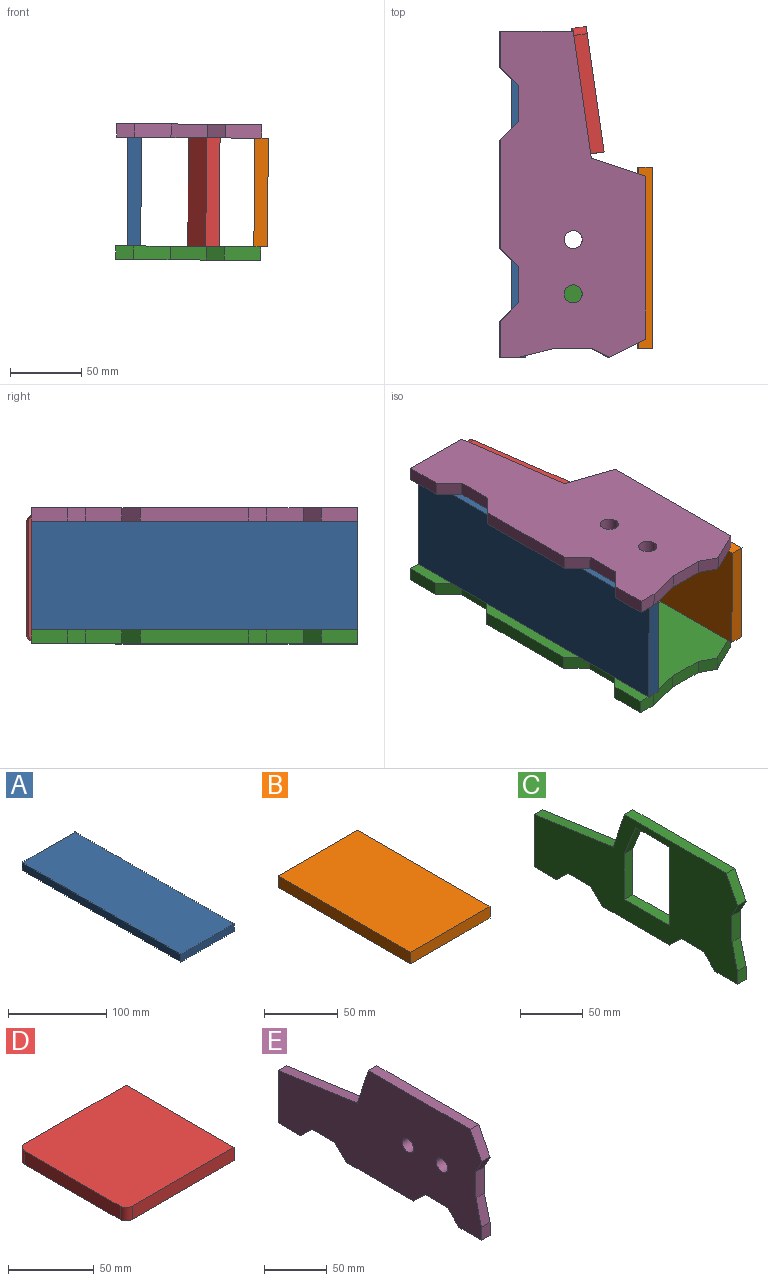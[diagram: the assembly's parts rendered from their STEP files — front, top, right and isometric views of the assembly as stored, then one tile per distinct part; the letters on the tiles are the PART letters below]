
ASSEMBLY  parts=5 mates=4
PART A: 6 faces, bbox 76.2x228.6x9.5 mm
  f0: plane 76.2x9.53mm, normal (0,-1,0), area 725.8mm2, adj f1,f3,f4,f5
  f1: plane 228.6x9.53mm, normal (1,0,0), area 2177.4mm2, adj f0,f2,f4,f5
  f2: plane 76.2x9.53mm, normal (0,1,0), area 725.8mm2, adj f1,f3,f4,f5
  f3: plane 228.6x9.53mm, normal (-1,0,0), area 2177.4mm2, adj f0,f2,f4,f5
  f4: plane 228.6x76.2mm, normal (0,0,1), area 17419.3mm2, adj f0,f1,f2,f3
  f5: plane 228.6x76.2mm, normal (0,0,-1), area 17419.3mm2, adj f0,f1,f2,f3
PART B: 6 faces, bbox 76.2x127x9.5 mm
  f0: plane 76.2x9.53mm, normal (0,1,0), area 725.8mm2, adj f1,f3,f4,f5
  f1: plane 127x9.53mm, normal (-1,0,0), area 1209.7mm2, adj f0,f2,f4,f5
  f2: plane 76.2x9.53mm, normal (0,-1,0), area 725.8mm2, adj f1,f3,f4,f5
  f3: plane 127x9.53mm, normal (1,0,0), area 1209.7mm2, adj f0,f2,f4,f5
  f4: plane 127x76.2mm, normal (0,0,1), area 9677.4mm2, adj f0,f1,f2,f3
  f5: plane 127x76.2mm, normal (0,0,-1), area 9677.4mm2, adj f0,f1,f2,f3
PART C: 25 faces, bbox 9.5x228.6x101.6 mm
  f0: plane 12.7x12.7mm, normal (0,0.71,-0.71), area 171.1mm2, adj f1,f22,f23,f24
  f1: plane 25.4x9.53mm, normal (0,0,-1), area 241.9mm2, adj f0,f2,f23,f24
  f2: plane 12.7x12.7mm, normal (0,-0.71,-0.71), area 171.1mm2, adj f1,f3,f23,f24
  f3: plane 25.4x9.53mm, normal (0,0,-1), area 241.9mm2, adj f2,f4,f23,f24
  f4: plane 50.8x9.53mm, normal (0,1,0), area 483.9mm2, adj f3,f5,f23,f24
  f5: plane 88.9x12.7mm, normal (0,0.14,0.99), area 855.4mm2, adj f4,f6,f23,f24
  f6: plane 38.1x12.7mm, normal (0,0.95,0.32), area 382.5mm2, adj f5,f7,f23,f24
  f7: plane 114.3x9.53mm, normal (0,0,1), area 1088.7mm2, adj f6,f8,f23,f24
  f8: plane 25.4x12.7mm, normal (0,-0.89,0.45), area 270.5mm2, adj f7,f9,f23,f24
  f9: plane 12.7x9.53mm, normal (0,-0.89,-0.45), area 135.2mm2, adj f8,f10,f23,f24
  f10: plane 25.4x9.53mm, normal (0,-1,0), area 241.9mm2, adj f9,f11,f23,f24
  f11: plane 25.4x9.53mm, normal (0,-0.97,0.24), area 249.4mm2, adj f10,f12,f23,f24
  f12: plane 12.7x9.53mm, normal (0,-1,0), area 121mm2, adj f11,f13,f23,f24
  f13: plane 25.4x9.53mm, normal (0,0,-1), area 241.9mm2, adj f12,f14,f23,f24
  f14: plane 12.7x12.7mm, normal (0,0.71,-0.71), area 171.1mm2, adj f13,f15,f23,f24
  f15: plane 25.4x9.53mm, normal (0,0,-1), area 241.9mm2, adj f14,f16,f23,f24
  f16: plane 12.7x12.7mm, normal (0,-0.71,-0.71), area 171.1mm2, adj f15,f22,f23,f24
  f17: plane 38.1x9.53mm, normal (0,0,-1), area 362.9mm2, adj f18,f21,f23,f24
  f18: plane 31.75x12.7mm, normal (0,-0.93,-0.37), area 325.7mm2, adj f17,f19,f23,f24
  f19: plane 44.45x9.53mm, normal (0,-1,0), area 423.4mm2, adj f18,f20,f23,f24
  f20: plane 50.8x9.53mm, normal (0,0,1), area 483.9mm2, adj f19,f21,f23,f24
  f21: plane 76.2x9.53mm, normal (0,1,0), area 725.8mm2, adj f17,f20,f23,f24
  f22: plane 76.2x9.53mm, normal (0,0,-1), area 725.8mm2, adj f0,f16,f23,f24
  f23: plane 228.6x101.6mm, normal (1,0,0), area 13951.6mm2, adj f0,f1,f2,f3,f4,f5,f6,f7
  f24: plane 228.6x101.6mm, normal (-1,0,0), area 13951.6mm2, adj f0,f1,f2,f3,f4,f5,f6,f7
PART D: 8 faces, bbox 88.9x88.9x9.5 mm
  f0: plane 83.82x9.53mm, normal (0,1,0), area 798.4mm2, adj f3,f4,f5,f6
  f1: plane 78.74x9.53mm, normal (-1,0,0), area 750mm2, adj f4,f5,f6,f7
  f2: plane 83.82x9.53mm, normal (0,-1,0), area 798.4mm2, adj f3,f4,f5,f7
  f3: plane 88.9x9.53mm, normal (1,0,0), area 846.8mm2, adj f0,f2,f4,f5
  f4: plane 88.9x88.9mm, normal (0,0,1), area 7892.1mm2, adj f0,f1,f2,f3,f6,f7
  f5: plane 88.9x88.9mm, normal (0,0,-1), area 7892.1mm2, adj f0,f1,f2,f3,f6,f7
  f6: cylinder r=5.08mm len=9.53mm, axis (0,0,1), area 76mm2, adj f0,f1,f4,f5
  f7: cylinder r=5.08mm len=9.53mm, axis (0,0,-1), area 76mm2, adj f1,f2,f4,f5
PART E: 22 faces, bbox 9.5x228.6x101.6 mm
  f0: plane 12.7x12.7mm, normal (0,0.71,-0.71), area 171.1mm2, adj f1,f19,f20,f21
  f1: plane 25.4x9.53mm, normal (0,0,-1), area 241.9mm2, adj f0,f2,f20,f21
  f2: plane 12.7x12.7mm, normal (0,-0.71,-0.71), area 171.1mm2, adj f1,f3,f20,f21
  f3: plane 25.4x9.53mm, normal (0,0,-1), area 241.9mm2, adj f2,f4,f20,f21
  f4: plane 50.8x9.53mm, normal (0,1,0), area 483.9mm2, adj f3,f5,f20,f21
  f5: plane 88.9x12.7mm, normal (0,0.14,0.99), area 855.4mm2, adj f4,f6,f20,f21
  f6: plane 38.1x12.7mm, normal (0,0.95,0.32), area 382.5mm2, adj f5,f7,f20,f21
  f7: plane 114.3x9.53mm, normal (0,0,1), area 1088.7mm2, adj f6,f8,f20,f21
  f8: plane 25.4x12.7mm, normal (0,-0.89,0.45), area 270.5mm2, adj f7,f9,f20,f21
  f9: plane 12.7x9.53mm, normal (0,-0.89,-0.45), area 135.2mm2, adj f8,f10,f20,f21
  f10: plane 25.4x9.53mm, normal (0,-1,0), area 241.9mm2, adj f9,f11,f20,f21
  f11: plane 25.4x9.53mm, normal (0,-0.97,0.24), area 249.4mm2, adj f10,f12,f20,f21
  f12: plane 12.7x9.53mm, normal (0,-1,0), area 121mm2, adj f11,f13,f20,f21
  f13: plane 25.4x9.53mm, normal (0,0,-1), area 241.9mm2, adj f12,f14,f20,f21
  f14: plane 12.7x12.7mm, normal (0,0.71,-0.71), area 171.1mm2, adj f13,f15,f20,f21
  f15: plane 25.4x9.53mm, normal (0,0,-1), area 241.9mm2, adj f14,f16,f20,f21
  f16: plane 12.7x12.7mm, normal (0,-0.71,-0.71), area 171.1mm2, adj f15,f19,f20,f21
  f17: cylinder r=6.35mm len=12.7mm, axis (-1,0,0), area 380mm2, adj f20,f21
  f18: cylinder r=6.35mm len=12.7mm, axis (-1,0,0), area 380mm2, adj f20,f21
  f19: plane 76.2x9.53mm, normal (0,0,-1), area 725.8mm2, adj f0,f16,f20,f21
  f20: plane 228.6x101.6mm, normal (1,0,0), area 17367.6mm2, adj f0,f1,f2,f3,f4,f5,f6,f7
  f21: plane 228.6x101.6mm, normal (-1,0,0), area 17367.6mm2, adj f0,f1,f2,f3,f4,f5,f6,f7
PLACE A rot(axis=(0,1,0),90.4deg) t=(-52.79,56.38,-10.26)mm
PLACE B rot(axis=(0,1,0),90.4deg) t=(36.11,11.93,-10.96)mm
PLACE C rot(axis=(0,1,0),90.4deg) t=(-19.95,25.28,-48.62)mm
PLACE D rot(axis=(0.63,-0.55,-0.55),115.2deg) t=(5.48,130.09,-12.31)mm
PLACE E rot(axis=(0,1,0),90.4deg) t=(-9.56,-0.78,37.03)mm fixed
MATE fastened D.f4 <-> E.f5  axis (-0.99,-0.14,0.01) through (-3.24,126.23,32.21)mm
MATE fastened B.f3 <-> C.f24  axis (-0.01,0,-1) through (40.57,11.93,-49.1)mm
MATE fastened A.f3 <-> E.f20  axis (0.01,0,1) through (-47.73,-57.92,27.8)mm
MATE fastened B.f1 <-> E.f20  axis (0.01,0,1) through (41.17,11.93,27.1)mm
